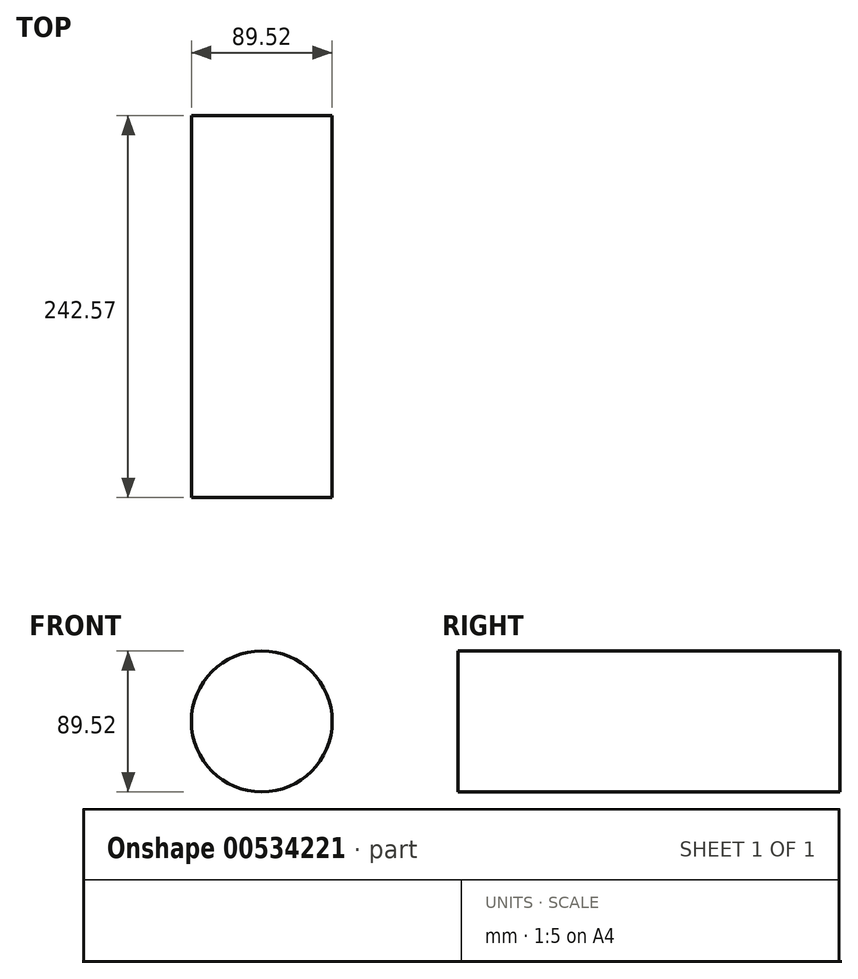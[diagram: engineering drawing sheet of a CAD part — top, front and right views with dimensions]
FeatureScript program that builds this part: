
annotation { "Feature Type Name" : "Feature", "Feature Type Description" : "" }
export const myFeature = defineFeature(function(context is Context, id is Id, definition is map)
    precondition{}
    {
        {
            var Q0;
            Q0=qCreatedBy(makeId("Front.planeOp"),FACE);
            var sketch = newSketch(context, id + "F0", { "sketchPlane" : qUnion([Q0])});
            skCircle(sketch, "E0", {"center": v(0, 0) * mm, "radius": 44.76 * mm});
            skSolve(sketch);
        }
        {
            var Q0;
            Q0=makeQuery(id+"F0.imprint","IMPRINT",FACE,{"disambiguationData":[TD([[makeQuery(id+"F0.imprint","IMPRINT",EDGE,{"derivedFrom":sQuery(id+"F0.wireOp",EDGE,"E0")}),1.0]])]});
            extrude(context, id + "F1", {"entities" : qUnion([Q0]), "depth" : 242.57 * mm, "offsetDistance" : 25.4 * mm});
        }
    });
